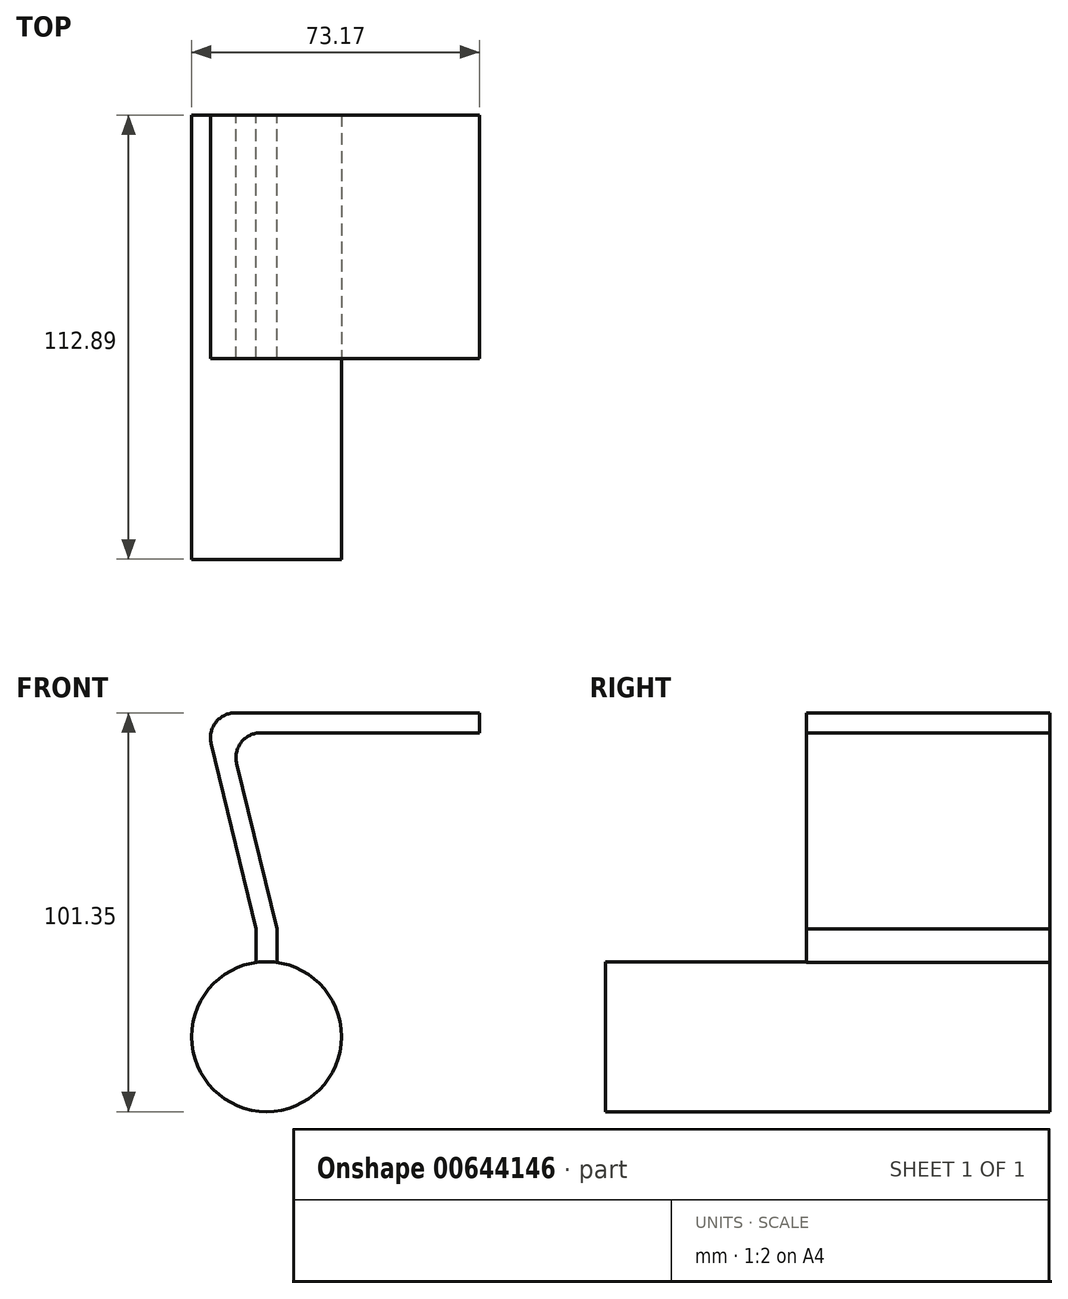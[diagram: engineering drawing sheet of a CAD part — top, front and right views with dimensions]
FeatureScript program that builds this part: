
annotation { "Feature Type Name" : "Feature", "Feature Type Description" : "" }
export const myFeature = defineFeature(function(context is Context, id is Id, definition is map)
    precondition{}
    {
        {
            var Q0;
            Q0=qCreatedBy(makeId("Top.planeOp"),FACE);
            var sketch = newSketch(context, id + "F0", { "sketchPlane" : qUnion([Q0])});
            skLineSegment(sketch, "E0.bottom", {"start": v(0, 0) * mm, "end": v(-70.09, 0) * mm});
            skLineSegment(sketch, "E0.top", {"start": v(0, 61.84) * mm, "end": v(-70.09, 61.84) * mm});
            skLineSegment(sketch, "E0.left", {"start": v(0, 0) * mm, "end": v(0, 61.84) * mm});
            skLineSegment(sketch, "E0.right", {"start": v(-70.09, 0) * mm, "end": v(-70.09, 61.84) * mm});
            skSolve(sketch);
        }
        {
            var Q0;
            Q0=makeQuery(id+"F0.imprint","IMPRINT",FACE,{"disambiguationData":[TD([[makeQuery(id+"F0.imprint","IMPRINT",EDGE,{"derivedFrom":sQuery(id+"F0.wireOp",EDGE,"E0.bottom")}),-1.0]])]});
            extrude(context, id + "F1", {"entities" : qUnion([Q0]), "oppositeDirection" : true, "depth" : 54.86 * mm, "offsetDistance" : 25.4 * mm});
        }
        {
            var Q0;
            Q0=makeQuery(id+"F1.opExtrude","SWEPT_FACE",FACE,{"disambiguationData":[OSD([sQuery(id+"F0.wireOp",EDGE,"E0.top")])]});
            var sketch = newSketch(context, id + "F2", { "sketchPlane" : qUnion([Q0])});
            skLineSegment(sketch, "E1", {"start": v(68.17, -7.85) * mm, "end": v(56.73, -54.86) * mm});
            skLineSegment(sketch, "E2", {"start": v(56.73, -54.86) * mm, "end": v(51.5, -54.86) * mm});
            skLineSegment(sketch, "E3", {"start": v(51.5, -54.86) * mm, "end": v(61.7, -12.93) * mm});
            skLineSegment(sketch, "E4", {"start": v(55.9, 0) * mm, "end": v(62, 0) * mm});
            skLineSegment(sketch, "E5", {"start": v(0, 0) * mm, "end": v(0, -5.08) * mm});
            skLineSegment(sketch, "E6", {"start": v(0, -5.08) * mm, "end": v(55.54, -5.08) * mm});
            skPoint(sketch, "E7.newPointA", {"position": v(64.86, 0) * mm});
            skPoint(sketch, "E8.visualSharp", {"position": v(70.09, 0) * mm});
            skLineSegment(sketch, "E9", {"start": v(68.17, -7.85) * mm, "end": v(68.17, -7.85) * mm});
            skLineSegment(sketch, "E10", {"start": v(52.67, -5.08) * mm, "end": v(55.54, -5.08) * mm});
            skLineSegment(sketch, "E11", {"start": v(61.7, -12.93) * mm, "end": v(61.7, -12.93) * mm});
            skPoint(sketch, "E12.start.orphan", {"position": v(62, -5.08) * mm});
            skPoint(sketch, "E13.orphan", {"position": v(68.17, -5.08) * mm});
            skPoint(sketch, "E14.visualSharp", {"position": v(63.62, -5.08) * mm});
            skArc(sketch, "E14.filletArc", {"start": v(61.7, -12.93) * mm, "mid": v(60.53, -7.5) * mm, "end": v(55.54, -5.08) * mm});
            skPoint(sketch, "E15.newPointB", {"position": v(62, 0) * mm});
            skArc(sketch, "E15.filletArc", {"start": v(68.17, -7.85) * mm, "mid": v(67, -2.43) * mm, "end": v(62, 0) * mm});
            skSolve(sketch);
        }
        {
            var Q0;
            {var subQ1=sQuery(id+"F2.wireOp",EDGE,"E3");Q0=makeQuery(id+"F2.imprint","IMPRINT",FACE,{"disambiguationData":[TD([[makeQuery(id+"F2.imprint","IMPRINT",EDGE,{"derivedFrom":subQ1}),1.0]])]});}
            var Q1;
            {var subQ4=sQuery(id+"F2.wireOp",EDGE,"E1");Q1=makeQuery(id+"F2.imprint","IMPRINT",FACE,{"disambiguationData":[TD([[makeQuery(id+"F2.imprint","IMPRINT",EDGE,{"derivedFrom":subQ4}),1.0]])]});}
            extrude(context, id + "F3", {"entities" : qUnion([Q0, Q1]), "operationType" : NewBodyOperationType.REMOVE, "endBound" : BoundingType.THROUGH_ALL, "oppositeDirection" : true, "depth" : 25.4 * mm, "offsetDistance" : 25.4 * mm});
        }
        {
            var Q0;
            Q0=makeQuery(id+"F1.opExtrude","CAP_FACE",FACE,{"disambiguationData":[OSD([sQuery(id+"F0.wireOp",EDGE,"E0.bottom"),sQuery(id+"F0.wireOp",EDGE,"E0.top"),sQuery(id+"F0.wireOp",EDGE,"E0.left"),sQuery(id+"F0.wireOp",EDGE,"E0.right")])],"isStart":false});
            var sketch = newSketch(context, id + "F4", { "sketchPlane" : qUnion([Q0])});
            skLineSegment(sketch, "E16.bottom", {"start": v(-56.73, -61.84) * mm, "end": v(-51.5, -61.84) * mm});
            skLineSegment(sketch, "E16.top", {"start": v(-56.73, 0) * mm, "end": v(-51.5, 0) * mm});
            skLineSegment(sketch, "E16.left", {"start": v(-56.73, -61.84) * mm, "end": v(-56.73, 0) * mm});
            skLineSegment(sketch, "E16.right", {"start": v(-51.5, -61.84) * mm, "end": v(-51.5, 0) * mm});
            skSolve(sketch);
        }
        {
            var Q0;
            Q0=makeQuery(id+"F4.imprint","IMPRINT",FACE,{"disambiguationData":[TD([[makeQuery(id+"F4.imprint","IMPRINT",EDGE,{"derivedFrom":sQuery(id+"F4.wireOp",EDGE,"E16.bottom")}),-1.0]])]});
            extrude(context, id + "F5", {"entities" : qUnion([Q0]), "operationType" : NewBodyOperationType.ADD, "depth" : 8.38 * mm, "offsetDistance" : 25.4 * mm});
        }
        {
            var Q0;
            Q0=makeQuery(id+"F5.opExtrude","CAP_FACE",FACE,{"disambiguationData":[OSD([sQuery(id+"F4.wireOp",EDGE,"E16.bottom"),sQuery(id+"F4.wireOp",EDGE,"E16.top"),sQuery(id+"F4.wireOp",EDGE,"E16.left"),sQuery(id+"F4.wireOp",EDGE,"E16.right")])],"isStart":false});
            var sketch = newSketch(context, id + "F6", { "sketchPlane" : qUnion([Q0])});
            skLineSegment(sketch, "E17.bottom", {"start": v(-51.5, -61.84) * mm, "end": v(-56.73, -61.84) * mm});
            skLineSegment(sketch, "E17.top", {"start": v(-51.5, 0) * mm, "end": v(-56.73, 0) * mm});
            skLineSegment(sketch, "E17.left", {"start": v(-51.5, -61.84) * mm, "end": v(-51.5, 0) * mm});
            skLineSegment(sketch, "E17.right", {"start": v(-56.73, -61.84) * mm, "end": v(-56.73, 0) * mm});
            skLineSegment(sketch, "E18.bottom", {"start": v(-51.5, -61.84) * mm, "end": v(-35.07, -61.84) * mm});
            skLineSegment(sketch, "E18.top", {"start": v(-51.5, 0) * mm, "end": v(-35.07, 0) * mm});
            skLineSegment(sketch, "E18.right", {"start": v(-35.07, -61.84) * mm, "end": v(-35.07, 0) * mm});
            skLineSegment(sketch, "E19.bottom", {"start": v(-73.17, 0) * mm, "end": v(-35.07, 0) * mm});
            skLineSegment(sketch, "E19.top", {"start": v(-73.17, -61.84) * mm, "end": v(-35.07, -61.84) * mm});
            skLineSegment(sketch, "E19.left", {"start": v(-73.17, 0) * mm, "end": v(-73.17, -61.84) * mm});
            skLineSegment(sketch, "E19.right", {"start": v(-35.07, 0) * mm, "end": v(-35.07, -61.84) * mm});
            skPoint(sketch, "E20", {"position": v(-51.5, -30.92) * mm});
            skPoint(sketch, "E21", {"position": v(-56.73, -30.92) * mm});
            skPoint(sketch, "E22", {"position": v(-54.12, -61.84) * mm});
            skSolve(sketch);
        }
        {
            var Q0;
            {var subQ0=sQuery(id+"F6.wireOp",EDGE,"E17.left");Q0=makeQuery(id+"F6.imprint","IMPRINT",FACE,{"disambiguationData":[TD([[makeQuery(id+"F6.imprint","IMPRINT",EDGE,{"derivedFrom":subQ0}),1.0]])]});}
            var Q1;
            {var subQ0=sQuery(id+"F6.wireOp",EDGE,"E17.right");Q1=makeQuery(id+"F6.imprint","IMPRINT",FACE,{"disambiguationData":[TD([[makeQuery(id+"F6.imprint","IMPRINT",EDGE,{"derivedFrom":subQ0}),1.0]])]});}
            var Q2;
            {var subQ0=sQuery(id+"F6.wireOp",EDGE,"E17.right");Q2=makeQuery(id+"F6.imprint","IMPRINT",FACE,{"disambiguationData":[TD([[makeQuery(id+"F6.imprint","IMPRINT",EDGE,{"derivedFrom":subQ0}),-1.0]])]});}
            extrude(context, id + "F7", {"entities" : qUnion([Q0, Q1, Q2]), "operationType" : NewBodyOperationType.ADD, "depth" : 38.1 * mm, "offsetDistance" : 25.4 * mm});
        }
        {
            var Q0;
            Q0=makeQuery(id+"F7.boolean.opBoolean","MERGE",FACE,{"derivedFrom":[makeQuery(id+"F5.boolean.opBoolean","MERGE",FACE,{"derivedFrom":[makeQuery(id+"F1.opExtrude","SWEPT_FACE",FACE,{"disambiguationData":[OSD([sQuery(id+"F0.wireOp",EDGE,"E0.bottom")])]}),makeQuery(id+"F5.opExtrude","SWEPT_FACE",FACE,{"disambiguationData":[OSD([sQuery(id+"F4.wireOp",EDGE,"E16.top")])]})]}),makeQuery(id+"F7.opExtrude","SWEPT_FACE",FACE,{"disambiguationData":[OSD([sQuery(id+"F6.wireOp",EDGE,"E19.bottom")])]})]});
            var sketch = newSketch(context, id + "F8", { "sketchPlane" : qUnion([Q0])});
            skPoint(sketch, "E23", {"position": v(-35.07, -82.3) * mm});
            skPoint(sketch, "E24", {"position": v(-73.17, -82.3) * mm});
            skPoint(sketch, "E25", {"position": v(-54.12, -101.35) * mm});
            skCircle(sketch, "E26", {"center": v(-54.12, -82.3) * mm, "radius": 19.05 * mm});
            skLineSegment(sketch, "E27", {"start": v(-51.5, -63.25) * mm, "end": v(-51.5, -64.6) * mm});
            skLineSegment(sketch, "E28", {"start": v(-56.73, -63.25) * mm, "end": v(-56.73, -66.35) * mm});
            skSolve(sketch);
        }
        {
            var Q0;
            {var subQ0=sQuery(id+"F8.wireOp",EDGE,"E27");var subQ1=sQuery(id+"F8.wireOp",EDGE,"E26");var subQ2=makeQuery(id+"F8.imprint","INTERSECT",VERTEX,{"derivedFrom":[subQ1,subQ0]});Q0=makeQuery(id+"F8.imprint","IMPRINT",FACE,{"disambiguationData":[TD([[makeQuery(id+"F8.imprint","IMPRINT",EDGE,{"disambiguationData":[TD([[subQ2,1.0]])],"derivedFrom":subQ1}),-1.0]])]});}
            var Q1;
            {var subQ0=sQuery(id+"F8.wireOp",EDGE,"E28");var subQ1=sQuery(id+"F8.wireOp",EDGE,"E26");var subQ2=makeQuery(id+"F8.imprint","INTERSECT",VERTEX,{"derivedFrom":[subQ1,subQ0]});Q1=makeQuery(id+"F8.imprint","IMPRINT",FACE,{"disambiguationData":[TD([[makeQuery(id+"F8.imprint","IMPRINT",EDGE,{"disambiguationData":[TD([[subQ2,-1.0]])],"derivedFrom":subQ1}),-1.0]])]});}
            var Q2;
            {var subQ0=sQuery(id+"F8.wireOp",EDGE,"E26");var subQ1=sQuery(id+"F6.wireOp",EDGE,"E19.bottom");var subQ4=makeQuery(id+"F7.opExtrude","CAP_EDGE",EDGE,{"disambiguationData":[OSD([subQ1])],"isStart":false});var subQ5=makeQuery(id+"F8.imprint","INTERSECT",VERTEX,{"derivedFrom":[subQ4,subQ0]});Q2=makeQuery(id+"F8.imprint","IMPRINT",FACE,{"disambiguationData":[TD([[makeQuery(id+"F8.imprint","IMPRINT",EDGE,{"disambiguationData":[TD([[subQ5,-1.0]])],"derivedFrom":subQ0}),-1.0]])]});}
            var Q3;
            {var subQ0=sQuery(id+"F8.wireOp",EDGE,"E26");var subQ1=sQuery(id+"F6.wireOp",EDGE,"E19.bottom");var subQ4=makeQuery(id+"F7.opExtrude","CAP_EDGE",EDGE,{"disambiguationData":[OSD([subQ1])],"isStart":false});var subQ5=makeQuery(id+"F8.imprint","INTERSECT",VERTEX,{"derivedFrom":[subQ4,subQ0]});Q3=makeQuery(id+"F8.imprint","IMPRINT",FACE,{"disambiguationData":[TD([[makeQuery(id+"F8.imprint","IMPRINT",EDGE,{"disambiguationData":[TD([[subQ5,1.0]])],"derivedFrom":subQ0}),-1.0]])]});}
            extrude(context, id + "F9", {"entities" : qUnion([Q0, Q1, Q2, Q3]), "operationType" : NewBodyOperationType.REMOVE, "oppositeDirection" : true, "depth" : 25.4 * mm, "offsetDistance" : 25.4 * mm});
        }
        {
            var Q0;
            Q0=makeQuery(id+"F9.boolean.opBoolean","COPY",FACE,{"derivedFrom":makeQuery(id+"F9.opExtrude","CAP_FACE",FACE,{"disambiguationData":[OSD([sQuery(id+"F6.wireOp",EDGE,"E19.bottom"),sQuery(id+"F6.wireOp",EDGE,"E19.right"),sQuery(id+"F8.wireOp",EDGE,"E26"),sQuery(id+"F8.wireOp",EDGE,"E27")])],"isStart":false})});
            var Q1;
            Q1=makeQuery(id+"F9.boolean.opBoolean","COPY",FACE,{"derivedFrom":makeQuery(id+"F9.opExtrude","CAP_FACE",FACE,{"disambiguationData":[OSD([sQuery(id+"F6.wireOp",EDGE,"E19.bottom"),sQuery(id+"F6.wireOp",EDGE,"E19.right"),sQuery(id+"F8.wireOp",EDGE,"E26")])],"isStart":false})});
            var Q2;
            Q2=makeQuery(id+"F9.boolean.opBoolean","COPY",FACE,{"derivedFrom":makeQuery(id+"F9.opExtrude","CAP_FACE",FACE,{"disambiguationData":[OSD([sQuery(id+"F6.wireOp",EDGE,"E19.bottom"),sQuery(id+"F6.wireOp",EDGE,"E19.left"),sQuery(id+"F8.wireOp",EDGE,"E26")])],"isStart":false})});
            var Q3;
            Q3=makeQuery(id+"F9.boolean.opBoolean","COPY",FACE,{"derivedFrom":makeQuery(id+"F9.opExtrude","CAP_FACE",FACE,{"disambiguationData":[OSD([sQuery(id+"F6.wireOp",EDGE,"E19.bottom"),sQuery(id+"F6.wireOp",EDGE,"E19.left"),sQuery(id+"F8.wireOp",EDGE,"E26"),sQuery(id+"F8.wireOp",EDGE,"E28")])],"isStart":false})});
            extrude(context, id + "F10", {"entities" : qUnion([Q0, Q1, Q2, Q3]), "operationType" : NewBodyOperationType.REMOVE, "endBound" : BoundingType.THROUGH_ALL, "oppositeDirection" : true, "depth" : 25.4 * mm, "offsetDistance" : 25.4 * mm});
        }
        {
            var Q0;
            Q0=makeQuery(id+"F7.boolean.opBoolean","MERGE",FACE,{"derivedFrom":[makeQuery(id+"F5.boolean.opBoolean","MERGE",FACE,{"derivedFrom":[makeQuery(id+"F1.opExtrude","SWEPT_FACE",FACE,{"disambiguationData":[OSD([sQuery(id+"F0.wireOp",EDGE,"E0.bottom")])]}),makeQuery(id+"F5.opExtrude","SWEPT_FACE",FACE,{"disambiguationData":[OSD([sQuery(id+"F4.wireOp",EDGE,"E16.top")])]})]}),makeQuery(id+"F7.opExtrude","SWEPT_FACE",FACE,{"disambiguationData":[OSD([sQuery(id+"F6.wireOp",EDGE,"E19.bottom")])]})]});
            var sketch = newSketch(context, id + "F11", { "sketchPlane" : qUnion([Q0])});
            skCircle(sketch, "E29", {"center": v(-54.12, -82.3) * mm, "radius": 19.05 * mm});
            skSolve(sketch);
        }
        {
            var Q0;
            {var subQ0=sQuery(id+"F11.wireOp",EDGE,"E29");var subQ1=sQuery(id+"F4.wireOp",EDGE,"E16.top");var subQ2=makeQuery(id+"F11.imprint","INTERSECT",VERTEX,{"derivedFrom":[makeQuery(id+"F9.boolean.opBoolean","MERGE",EDGE,{"derivedFrom":[makeQuery(id+"F5.opExtrude","SWEPT_EDGE",EDGE,{"disambiguationData":[OSD([subQ1,sQuery(id+"F4.wireOp",EDGE,"E16.right")])]}),makeQuery(id+"F9.opExtrude","CAP_EDGE",EDGE,{"disambiguationData":[OSD([sQuery(id+"F8.wireOp",EDGE,"E27")])],"isStart":true})]}),subQ0]});Q0=makeQuery(id+"F11.imprint","IMPRINT",FACE,{"disambiguationData":[TD([[makeQuery(id+"F11.imprint","IMPRINT",EDGE,{"disambiguationData":[TD([[subQ2,-1.0]])],"derivedFrom":subQ0}),1.0]])]});}
            extrude(context, id + "F12", {"entities" : qUnion([Q0]), "operationType" : NewBodyOperationType.ADD, "depth" : 51.05 * mm, "offsetDistance" : 25.4 * mm});
        }
    });
